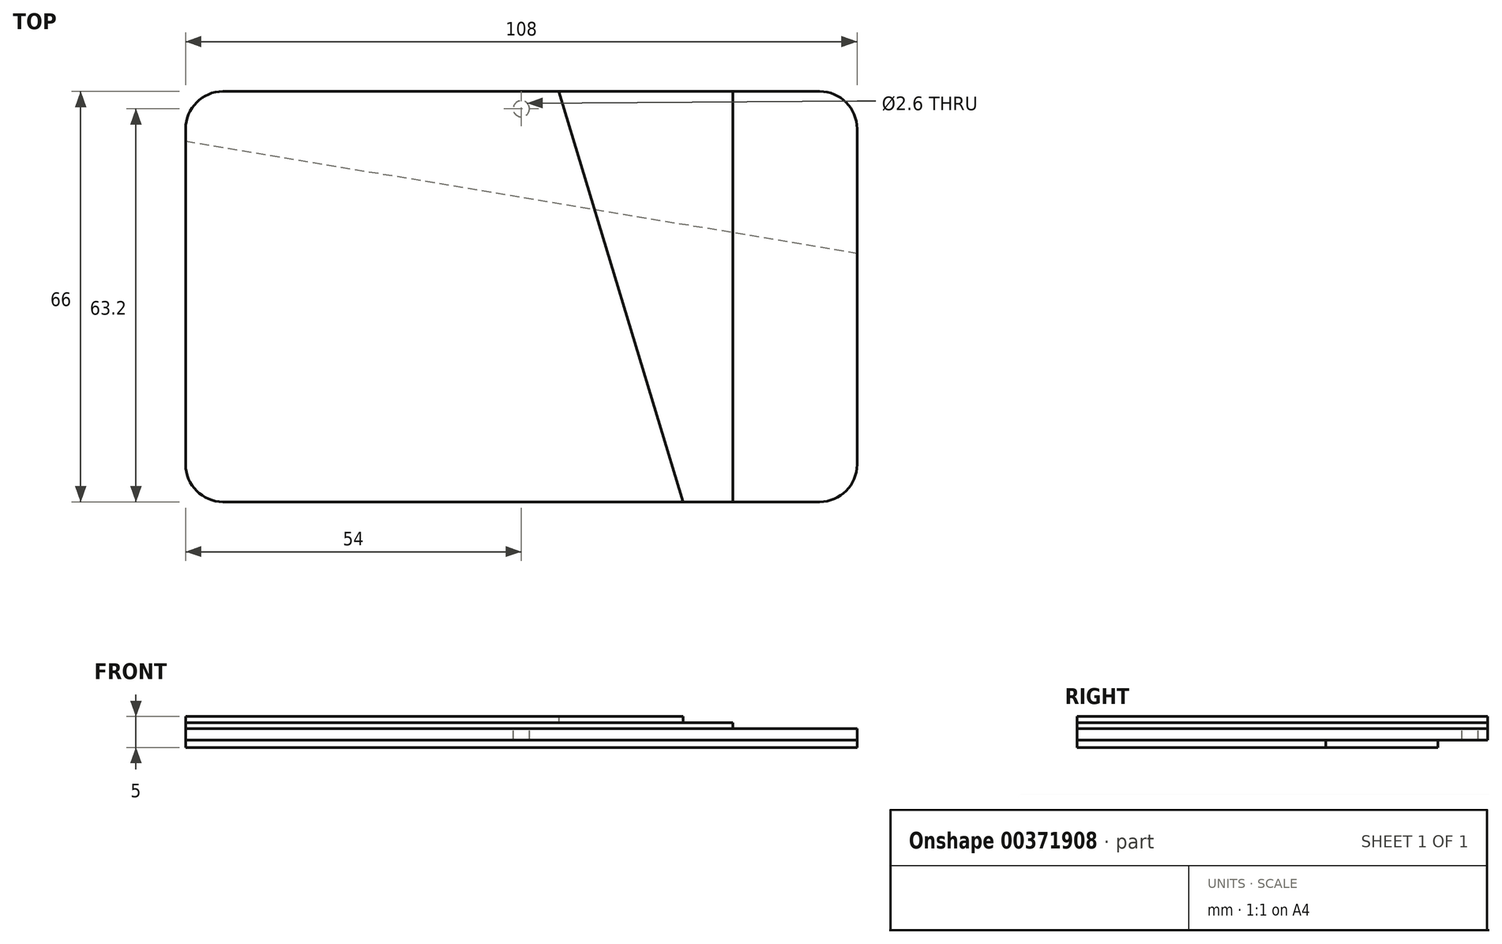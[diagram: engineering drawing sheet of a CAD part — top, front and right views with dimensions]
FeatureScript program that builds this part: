
annotation { "Feature Type Name" : "Feature", "Feature Type Description" : "" }
export const myFeature = defineFeature(function(context is Context, id is Id, definition is map)
    precondition{}
    {
        {
            var Q0;
            Q0=qCreatedBy(makeId("Top.planeOp"),FACE);
            var sketch = newSketch(context, id + "F0", { "sketchPlane" : qUnion([Q0])});
            skLineSegment(sketch, "E0.bottom", {"start": v(-48, -27) * mm, "end": v(48, -27) * mm, "construction": true});
            skLineSegment(sketch, "E0.top", {"start": v(-48, 27) * mm, "end": v(48, 27) * mm, "construction": true});
            skLineSegment(sketch, "E0.left", {"start": v(-48, -27) * mm, "end": v(-48, 27) * mm, "construction": true});
            skLineSegment(sketch, "E0.right", {"start": v(48, -27) * mm, "end": v(48, 27) * mm, "construction": true});
            skPoint(sketch, "E0.middle", {"position": v(0, 0) * mm});
            skLineSegment(sketch, "E1.bottom", {"start": v(-54, 33) * mm, "end": v(54, 33) * mm});
            skLineSegment(sketch, "E1.top", {"start": v(-54, -33) * mm, "end": v(54, -33) * mm});
            skLineSegment(sketch, "E1.left", {"start": v(-54, 33) * mm, "end": v(-54, -33) * mm});
            skLineSegment(sketch, "E1.right", {"start": v(54, 33) * mm, "end": v(54, -33) * mm});
            skSolve(sketch);
        }
        {
            var Q0;
            Q0 = qSketchRegion(id + "F0", true);
            extrude(context, id + "F1", {"entities" : qUnion([Q0]), "depth" : 1.8 * mm});
        }
        {
            var Q0;
            Q0=makeQuery(id+"F1.opExtrude","CAP_FACE",FACE,{"disambiguationData":[OSD([sQuery(id+"F0.wireOp",EDGE,"E1.bottom"),sQuery(id+"F0.wireOp",EDGE,"E1.top"),sQuery(id+"F0.wireOp",EDGE,"E1.left"),sQuery(id+"F0.wireOp",EDGE,"E1.right")])],"isStart":true});
            var sketch = newSketch(context, id + "F2", { "sketchPlane" : qUnion([Q0])});
            skLineSegment(sketch, "E2", {"start": v(-54, -25) * mm, "end": v(54, -7) * mm});
            skLineSegment(sketch, "E3", {"start": v(-54, -25) * mm, "end": v(-54, 33) * mm});
            skLineSegment(sketch, "E4", {"start": v(-54, 33) * mm, "end": v(54, 33) * mm});
            skLineSegment(sketch, "E5", {"start": v(54, 33) * mm, "end": v(54, -7) * mm});
            skSolve(sketch);
        }
        {
            var Q0;
            Q0 = qSketchRegion(id + "F2", true);
            extrude(context, id + "F3", {"entities" : qUnion([Q0]), "depth" : 1.2 * mm});
        }
        {
            var Q0;
            Q0=makeQuery(id+"F1.opExtrude","CAP_FACE",FACE,{"disambiguationData":[OSD([sQuery(id+"F0.wireOp",EDGE,"E1.bottom"),sQuery(id+"F0.wireOp",EDGE,"E1.top"),sQuery(id+"F0.wireOp",EDGE,"E1.left"),sQuery(id+"F0.wireOp",EDGE,"E1.right")])],"isStart":false});
            var sketch = newSketch(context, id + "F4", { "sketchPlane" : qUnion([Q0])});
            skLineSegment(sketch, "E6", {"start": v(34, 33) * mm, "end": v(34, -33) * mm});
            skLineSegment(sketch, "E7", {"start": v(34, -33) * mm, "end": v(-54, -33) * mm});
            skLineSegment(sketch, "E8", {"start": v(-54, -33) * mm, "end": v(-54, 33) * mm});
            skLineSegment(sketch, "E9", {"start": v(-54, 33) * mm, "end": v(34, 33) * mm});
            skSolve(sketch);
        }
        {
            var Q0;
            Q0 = qSketchRegion(id + "F4", true);
            extrude(context, id + "F5", {"entities" : qUnion([Q0]), "depth" : 1 * mm});
        }
        {
            var Q0;
            Q0=makeQuery(id+"F5.opExtrude","CAP_FACE",FACE,{"disambiguationData":[OSD([sQuery(id+"F4.wireOp",EDGE,"E6"),sQuery(id+"F4.wireOp",EDGE,"E7"),sQuery(id+"F4.wireOp",EDGE,"E8"),sQuery(id+"F4.wireOp",EDGE,"E9")])],"isStart":false});
            var sketch = newSketch(context, id + "F6", { "sketchPlane" : qUnion([Q0])});
            skLineSegment(sketch, "E10", {"start": v(-54, 33) * mm, "end": v(-54, -33) * mm});
            skLineSegment(sketch, "E11", {"start": v(-54, -33) * mm, "end": v(34, -33) * mm});
            skLineSegment(sketch, "E12", {"start": v(26, -33) * mm, "end": v(6, 33) * mm});
            skLineSegment(sketch, "E13", {"start": v(6, 33) * mm, "end": v(-54, 33) * mm});
            skSolve(sketch);
        }
        {
            var Q0;
            Q0 = qSketchRegion(id + "F6", true);
            extrude(context, id + "F7", {"entities" : qUnion([Q0]), "depth" : 1 * mm});
        }
        {
            var Q0;
            Q0=makeQuery(id+"F1.opExtrude","SWEPT_EDGE",EDGE,{"disambiguationData":[OSD([sQuery(id+"F0.wireOp",EDGE,"E1.bottom"),sQuery(id+"F0.wireOp",EDGE,"E1.left")])]});
            var Q1;
            Q1=makeQuery(id+"F5.opExtrude","SWEPT_EDGE",EDGE,{"disambiguationData":[OSD([sQuery(id+"F4.wireOp",EDGE,"E8"),sQuery(id+"F4.wireOp",EDGE,"E9")])]});
            var Q2;
            Q2=makeQuery(id+"F7.opExtrude","SWEPT_EDGE",EDGE,{"disambiguationData":[OSD([sQuery(id+"F6.wireOp",EDGE,"E10"),sQuery(id+"F6.wireOp",EDGE,"E13")])]});
            var Q3;
            Q3=makeQuery(id+"F1.opExtrude","SWEPT_EDGE",EDGE,{"disambiguationData":[OSD([sQuery(id+"F0.wireOp",EDGE,"E1.top"),sQuery(id+"F0.wireOp",EDGE,"E1.left")])]});
            var Q4;
            Q4=makeQuery(id+"F5.opExtrude","SWEPT_EDGE",EDGE,{"disambiguationData":[OSD([sQuery(id+"F4.wireOp",EDGE,"E7"),sQuery(id+"F4.wireOp",EDGE,"E8")])]});
            var Q5;
            Q5=makeQuery(id+"F7.opExtrude","SWEPT_EDGE",EDGE,{"disambiguationData":[OSD([sQuery(id+"F6.wireOp",EDGE,"E10"),sQuery(id+"F6.wireOp",EDGE,"E11")])]});
            var Q6;
            Q6=makeQuery(id+"F3.opExtrude","SWEPT_EDGE",EDGE,{"disambiguationData":[OSD([sQuery(id+"F2.wireOp",EDGE,"E3"),sQuery(id+"F2.wireOp",EDGE,"E4")])]});
            var Q7;
            Q7=makeQuery(id+"F1.opExtrude","SWEPT_EDGE",EDGE,{"disambiguationData":[OSD([sQuery(id+"F0.wireOp",EDGE,"E1.top"),sQuery(id+"F0.wireOp",EDGE,"E1.right")])]});
            var Q8;
            Q8=makeQuery(id+"F3.opExtrude","SWEPT_EDGE",EDGE,{"disambiguationData":[OSD([sQuery(id+"F2.wireOp",EDGE,"E4"),sQuery(id+"F2.wireOp",EDGE,"E5")])]});
            var Q9;
            Q9=makeQuery(id+"F1.opExtrude","SWEPT_EDGE",EDGE,{"disambiguationData":[OSD([sQuery(id+"F0.wireOp",EDGE,"E1.bottom"),sQuery(id+"F0.wireOp",EDGE,"E1.right")])]});
            fillet(context, id + "F8", {"entities" : qUnion([Q0, Q1, Q2, Q3, Q4, Q5, Q6, Q7, Q8, Q9]), "radius" : 6 * mm, "tangentPropagation" : true, "allowEdgeOverflow" : false});
        }
        {
            var Q0;
            Q0=makeQuery(id+"F1.opExtrude","CAP_FACE",FACE,{"disambiguationData":[OSD([sQuery(id+"F0.wireOp",EDGE,"E1.bottom"),sQuery(id+"F0.wireOp",EDGE,"E1.top"),sQuery(id+"F0.wireOp",EDGE,"E1.left"),sQuery(id+"F0.wireOp",EDGE,"E1.right")])],"isStart":false});
            var sketch = newSketch(context, id + "F9", { "sketchPlane" : qUnion([Q0])});
            skCircle(sketch, "E14", {"center": v(0, 30.2) * mm, "radius": 1.3 * mm});
            skPoint(sketch, "E14.centerSnap0", {"position": v(0, 33) * mm});
            skSolve(sketch);
        }
        {
            var Q0;
            Q0 = qSketchRegion(id + "F9", true);
            extrude(context, id + "F10", {"entities" : qUnion([Q0]), "operationType" : NewBodyOperationType.REMOVE, "oppositeDirection" : true, "depth" : 25 * mm});
        }
    });
